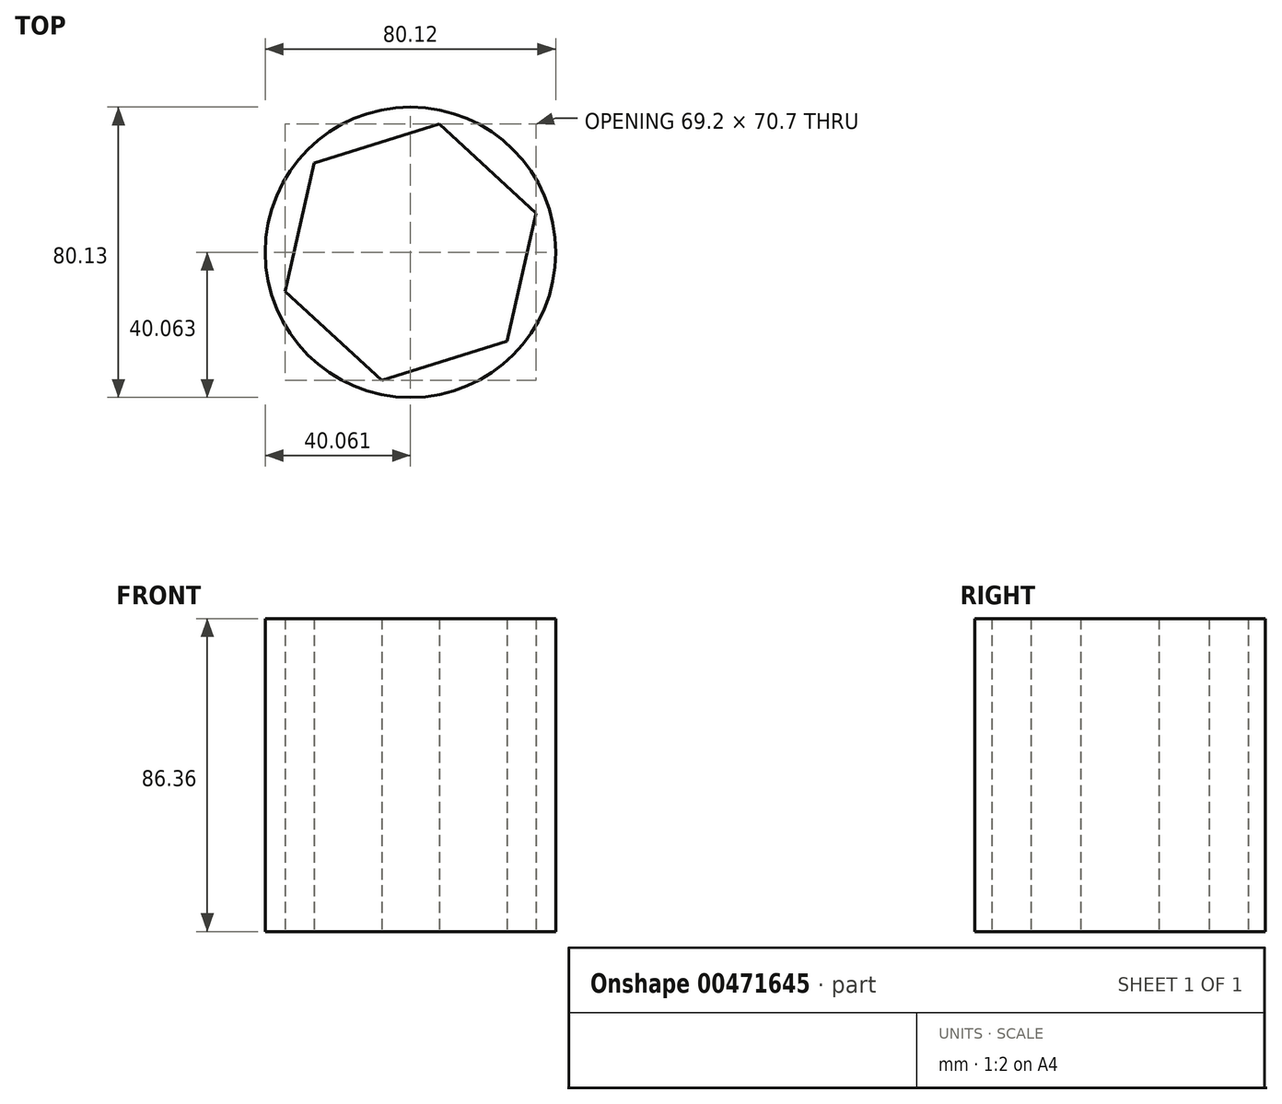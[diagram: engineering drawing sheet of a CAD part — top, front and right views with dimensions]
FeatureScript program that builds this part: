
annotation { "Feature Type Name" : "Feature", "Feature Type Description" : "" }
export const myFeature = defineFeature(function(context is Context, id is Id, definition is map)
    precondition{}
    {
        {
            var Q0;
            Q0=qCreatedBy(makeId("Top.planeOp"),FACE);
            var sketch = newSketch(context, id + "F0", { "sketchPlane" : qUnion([Q0])});
            skCircle(sketch, "E0", {"center": v(-9.32, 6.52) * mm, "radius": 40.06 * mm});
            skCircle(sketch, "E1.cCircle", {"center": v(-9.32, 6.52) * mm, "radius": 31.38 * mm, "construction": true});
            skLineSegment(sketch, "E1.0", {"start": v(-35.95, 31.1) * mm, "end": v(-1.35, 41.87) * mm});
            skLineSegment(sketch, "E1.1", {"start": v(-1.35, 41.87) * mm, "end": v(25.28, 17.3) * mm});
            skLineSegment(sketch, "E1.2", {"start": v(25.28, 17.3) * mm, "end": v(17.31, -18.05) * mm});
            skLineSegment(sketch, "E1.3", {"start": v(17.31, -18.05) * mm, "end": v(-17.28, -28.83) * mm});
            skLineSegment(sketch, "E1.4", {"start": v(-17.28, -28.83) * mm, "end": v(-43.92, -4.25) * mm});
            skLineSegment(sketch, "E1.5", {"start": v(-43.92, -4.25) * mm, "end": v(-35.95, 31.1) * mm});
            skPoint(sketch, "E1.0.midPoint", {"position": v(-18.65, 36.49) * mm});
            skSolve(sketch);
        }
        {
            var Q0;
            Q0=qCreatedBy(makeId("Top.planeOp"),FACE);
            cPlane(context, id + "F1", {"entities" : qUnion([Q0]), "cplaneType" : CPlaneType.OFFSET, "offset" : 50.8 * mm, "width" : 152.4 * mm, "height" : 152.4 * mm});
        }
        {
            var Q0;
            Q0=makeQuery(id+"F0.imprint","IMPRINT",FACE,{"disambiguationData":[TD([[makeQuery(id+"F0.imprint","IMPRINT",EDGE,{"derivedFrom":sQuery(id+"F0.wireOp",EDGE,"E0")}),1.0]])]});
            extrude(context, id + "F2", {"entities" : qUnion([Q0]), "depth" : 86.36 * mm});
        }
    });
